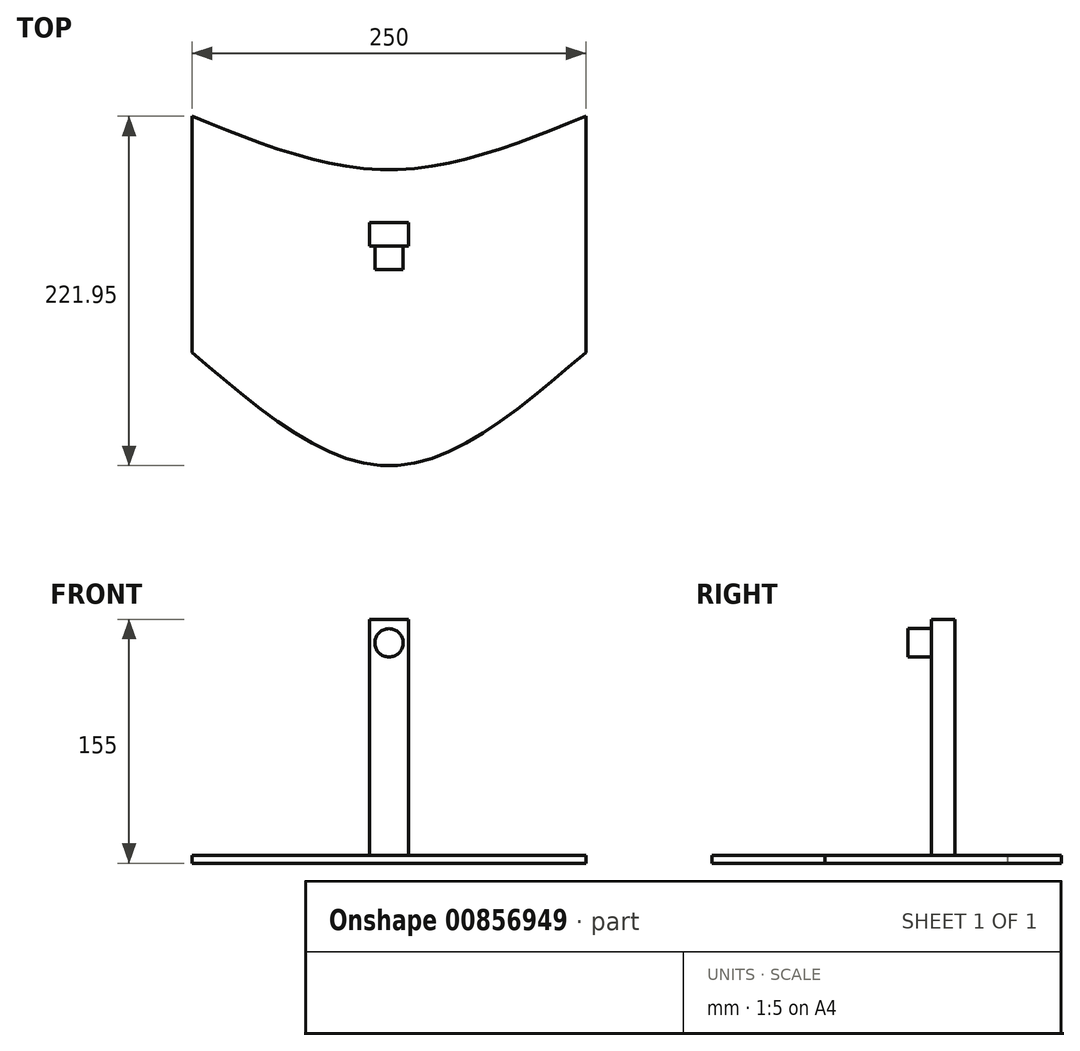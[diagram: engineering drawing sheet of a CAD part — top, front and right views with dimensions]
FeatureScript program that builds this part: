
annotation { "Feature Type Name" : "Feature", "Feature Type Description" : "" }
export const myFeature = defineFeature(function(context is Context, id is Id, definition is map)
    precondition{}
    {
        {
            var Q0;
            Q0=qCreatedBy(makeId("Top.planeOp"),FACE);
            var sketch = newSketch(context, id + "F0", { "sketchPlane" : qUnion([Q0])});
            skLineSegment(sketch, "E0.left", {"start": v(-125, 75) * mm, "end": v(-125, -75) * mm});
            skLineSegment(sketch, "E0.right", {"start": v(125, 75) * mm, "end": v(125, -75) * mm});
            skFitSpline(sketch, "E1", {"points": [v(-125, -75) * mm, v(0, -146.95) * mm, v(125, -75) * mm], "startDerivative": vector(250, -215.85) * mm, "endDerivative": vector(250, 215.85) * mm});
            skFitSpline(sketch, "E2", {"points": [v(-125, 75) * mm, v(0, 41.04) * mm, v(125, 75) * mm], "startDerivative": vector(250, -101.9) * mm, "endDerivative": vector(250, 101.9) * mm});
            skSolve(sketch);
        }
        {
            var Q0;
            Q0=makeQuery(id+"F0.imprint","IMPRINT",FACE,{"disambiguationData":[TD([[makeQuery(id+"F0.imprint","IMPRINT",EDGE,{"derivedFrom":sQuery(id+"F0.wireOp",EDGE,"E0.left")}),1.0]])]});
            extrude(context, id + "F1", {"entities" : qUnion([Q0]), "depth" : 5 * mm, "offsetDistance" : 25 * mm});
        }
        {
            var Q0;
            Q0=makeQuery(id+"F1.opExtrude","CAP_FACE",FACE,{"disambiguationData":[OSD([sQuery(id+"F0.wireOp",EDGE,"E0.left"),sQuery(id+"F0.wireOp",EDGE,"E0.right"),sQuery(id+"F0.wireOp",EDGE,"E1"),sQuery(id+"F0.wireOp",EDGE,"E2")])],"isStart":false});
            var sketch = newSketch(context, id + "F2", { "sketchPlane" : qUnion([Q0])});
            skLineSegment(sketch, "E3.bottom", {"start": v(12.5, -7.5) * mm, "end": v(-12.5, -7.5) * mm});
            skLineSegment(sketch, "E3.top", {"start": v(12.5, 7.5) * mm, "end": v(-12.5, 7.5) * mm});
            skLineSegment(sketch, "E3.left", {"start": v(12.5, -7.5) * mm, "end": v(12.5, 7.5) * mm});
            skLineSegment(sketch, "E3.right", {"start": v(-12.5, -7.5) * mm, "end": v(-12.5, 7.5) * mm});
            skPoint(sketch, "E3.middle", {"position": v(0, 0) * mm});
            skSolve(sketch);
        }
        {
            var Q0;
            Q0=makeQuery(id+"F2.imprint","IMPRINT",FACE,{"disambiguationData":[TD([[makeQuery(id+"F2.imprint","IMPRINT",EDGE,{"derivedFrom":sQuery(id+"F2.wireOp",EDGE,"E3.bottom")}),-1.0]])]});
            extrude(context, id + "F3", {"entities" : qUnion([Q0]), "operationType" : NewBodyOperationType.ADD, "depth" : 150 * mm, "offsetDistance" : 25 * mm});
        }
        {
            var Q0;
            Q0=makeQuery(id+"F3.opExtrude","SWEPT_FACE",FACE,{"disambiguationData":[OSD([sQuery(id+"F2.wireOp",EDGE,"E3.bottom")])]});
            var sketch = newSketch(context, id + "F4", { "sketchPlane" : qUnion([Q0])});
            skCircle(sketch, "E4", {"center": v(0, 140) * mm, "radius": 9 * mm});
            skSolve(sketch);
        }
        {
            var Q0;
            Q0=makeQuery(id+"F4.imprint","IMPRINT",FACE,{"disambiguationData":[TD([[makeQuery(id+"F4.imprint","IMPRINT",EDGE,{"derivedFrom":sQuery(id+"F4.wireOp",EDGE,"E4")}),1.0]])]});
            extrude(context, id + "F5", {"entities" : qUnion([Q0]), "depth" : 15 * mm, "offsetDistance" : 25 * mm});
        }
    });
